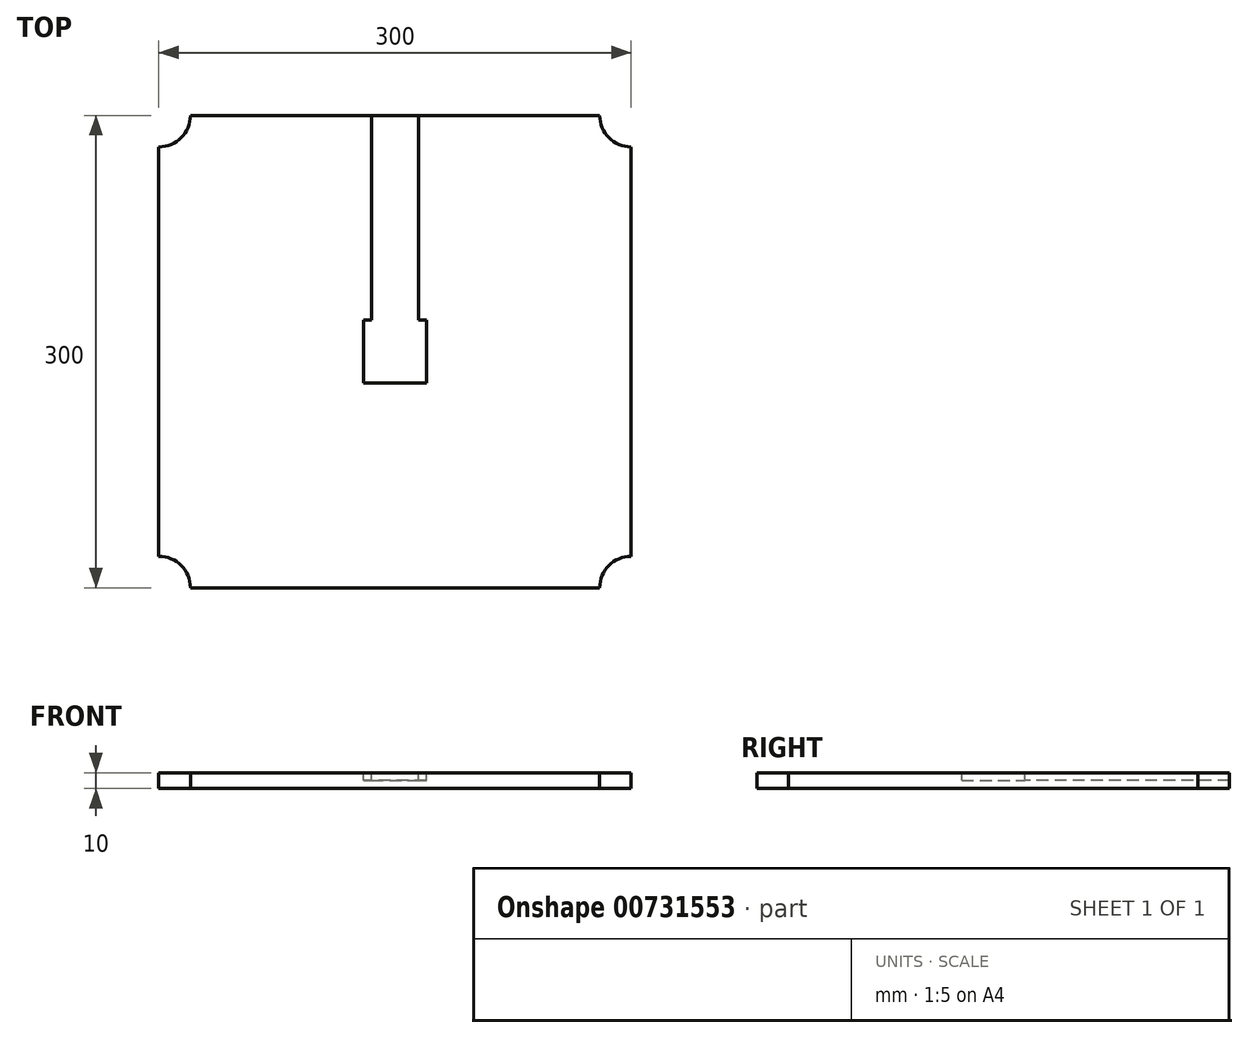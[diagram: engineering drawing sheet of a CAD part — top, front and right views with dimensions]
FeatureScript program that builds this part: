
annotation { "Feature Type Name" : "Feature", "Feature Type Description" : "" }
export const myFeature = defineFeature(function(context is Context, id is Id, definition is map)
    precondition{}
    {
        {
            var Q0;
            Q0=qCreatedBy(makeId("Top.planeOp"),FACE);
            var sketch = newSketch(context, id + "F0", { "sketchPlane" : qUnion([Q0])});
            skCircle(sketch, "E0.cCircle", {"center": v(0, 0) * mm, "radius": 150 * mm, "construction": true});
            skLineSegment(sketch, "E0.0", {"start": v(-130, 150) * mm, "end": v(130, 150) * mm});
            skLineSegment(sketch, "E0.1", {"start": v(150, 130) * mm, "end": v(150, -130) * mm});
            skLineSegment(sketch, "E0.2", {"start": v(130, -150) * mm, "end": v(-130, -150) * mm});
            skLineSegment(sketch, "E0.3", {"start": v(-150, -130) * mm, "end": v(-150, 130) * mm});
            skPoint(sketch, "E0.0.midPoint", {"position": v(0, 150) * mm});
            skArc(sketch, "E1", {"start": v(-150, 130) * mm, "mid": v(-135.86, 135.86) * mm, "end": v(-130, 150) * mm});
            skArc(sketch, "E2", {"start": v(130, 150) * mm, "mid": v(135.86, 135.86) * mm, "end": v(150, 130) * mm});
            skArc(sketch, "E3", {"start": v(150, -130) * mm, "mid": v(135.86, -135.86) * mm, "end": v(130, -150) * mm});
            skArc(sketch, "E4", {"start": v(-130, -150) * mm, "mid": v(-135.86, -135.86) * mm, "end": v(-150, -130) * mm});
            skSolve(sketch);
        }
        {
            var Q0;
            Q0=qCreatedBy(makeId("Top.planeOp"),FACE);
            var sketch = newSketch(context, id + "F1", { "sketchPlane" : qUnion([Q0])});
            skCircle(sketch, "E5.cCircle", {"center": v(0, 0) * mm, "radius": 20 * mm, "construction": true});
            skLineSegment(sketch, "E5.0", {"start": v(-20, 20) * mm, "end": v(20, 20) * mm});
            skLineSegment(sketch, "E5.1", {"start": v(20, 20) * mm, "end": v(20, -20) * mm});
            skLineSegment(sketch, "E5.2", {"start": v(20, -20) * mm, "end": v(-20, -20) * mm});
            skLineSegment(sketch, "E5.3", {"start": v(-20, -20) * mm, "end": v(-20, 20) * mm});
            skPoint(sketch, "E5.0.midPoint", {"position": v(0, 20) * mm});
            skLineSegment(sketch, "E6", {"start": v(-15, 20) * mm, "end": v(-15, 150) * mm});
            skLineSegment(sketch, "E7", {"start": v(-15, 150) * mm, "end": v(15, 150) * mm});
            skLineSegment(sketch, "E8", {"start": v(15, 150) * mm, "end": v(15, 20) * mm});
            skSolve(sketch);
        }
        {
            var Q0;
            Q0=makeQuery(id+"F0.imprint","IMPRINT",FACE,{"disambiguationData":[TD([[makeQuery(id+"F0.imprint","IMPRINT",EDGE,{"derivedFrom":sQuery(id+"F0.wireOp",EDGE,"E0.0")}),-1.0]])]});
            extrude(context, id + "F2", {"entities" : qUnion([Q0]), "oppositeDirection" : true, "depth" : 10 * mm, "offsetDistance" : 25 * mm});
        }
        {
            var Q0;
            Q0 = qSketchRegion(id + "F1", true);
            extrude(context, id + "F3", {"entities" : qUnion([Q0]), "operationType" : NewBodyOperationType.REMOVE, "oppositeDirection" : true, "depth" : 5 * mm, "offsetDistance" : 25 * mm});
        }
    });
